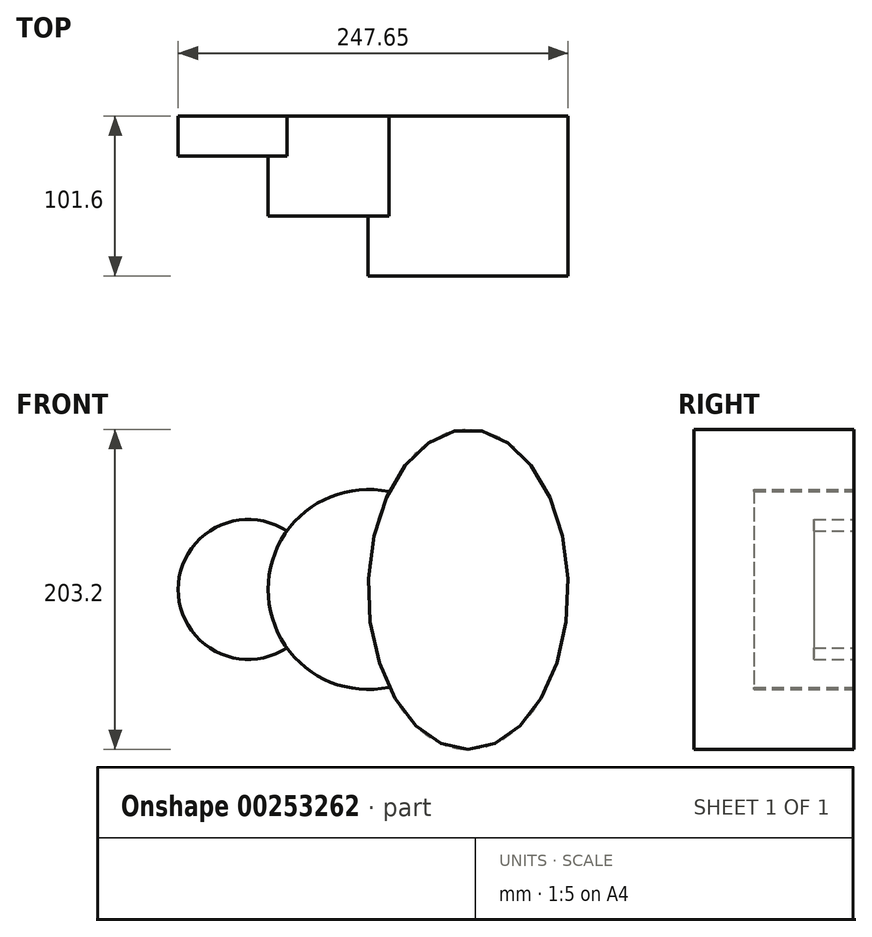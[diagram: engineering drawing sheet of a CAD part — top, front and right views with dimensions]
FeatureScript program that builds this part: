
annotation { "Feature Type Name" : "Feature", "Feature Type Description" : "" }
export const myFeature = defineFeature(function(context is Context, id is Id, definition is map)
    precondition{}
    {
        {
            var Q0;
            Q0=qCreatedBy(makeId("Front.planeOp"),FACE);
            var sketch = newSketch(context, id + "F0", { "sketchPlane" : qUnion([Q0])});
            skLineSegment(sketch, "E0", {"start": v(0, 0) * mm, "end": v(-76.2, 0) * mm, "construction": true});
            skCircle(sketch, "E1", {"center": v(-76.2, 0) * mm, "radius": 44.45 * mm});
            skPoint(sketch, "E2", {"position": v(-63.5, 0) * mm});
            skPoint(sketch, "E3", {"position": v(-31.75, 0) * mm});
            skCircle(sketch, "E4", {"center": v(0, 0) * mm, "radius": 63.5 * mm});
            skPoint(sketch, "E5", {"position": v(63.5, 0) * mm});
            skLineSegment(sketch, "E6", {"start": v(63.5, 0) * mm, "end": v(63.5, 101.6) * mm, "construction": true});
            skEllipse(sketch, "E7", {"center": v(63.5, 0) * mm, "majorRadius": 63.5 * mm, "minorRadius": 101.6 * mm, "majorAxis": v(-1, 0)});
            skSolve(sketch);
        }
        {
            var Q0;
            {var subQ0=sQuery(id+"F0.wireOp",EDGE,"E4");var subQ1=sQuery(id+"F0.wireOp",EDGE,"E1");var subQ2=makeQuery(id+"F0.imprint","INTERSECT",VERTEX,{"disambiguationData":[OD(0.0)],"derivedFrom":[subQ1,subQ0]});Q0=makeQuery(id+"F0.imprint","IMPRINT",FACE,{"disambiguationData":[TD([[makeQuery(id+"F0.imprint","IMPRINT",EDGE,{"disambiguationData":[TD([[subQ2,-1.0]])],"derivedFrom":subQ1}),1.0]])]});}
            extrude(context, id + "F1", {"entities" : qUnion([Q0]), "depth" : 25.4 * mm});
        }
        {
            var Q0;
            {var subQ0=sQuery(id+"F0.wireOp",EDGE,"E4");var subQ1=sQuery(id+"F0.wireOp",EDGE,"E1");var subQ2=makeQuery(id+"F0.imprint","INTERSECT",VERTEX,{"disambiguationData":[OD(0.0)],"derivedFrom":[subQ1,subQ0]});Q0=makeQuery(id+"F0.imprint","IMPRINT",FACE,{"disambiguationData":[TD([[makeQuery(id+"F0.imprint","IMPRINT",EDGE,{"disambiguationData":[TD([[subQ2,1.0]])],"derivedFrom":subQ1}),1.0]])]});}
            var Q1;
            {var subQ0=sQuery(id+"F0.wireOp",EDGE,"E4");var subQ1=sQuery(id+"F0.wireOp",EDGE,"E1");var subQ2=makeQuery(id+"F0.imprint","INTERSECT",VERTEX,{"disambiguationData":[OD(0.0)],"derivedFrom":[subQ1,subQ0]});Q1=makeQuery(id+"F0.imprint","IMPRINT",FACE,{"disambiguationData":[TD([[makeQuery(id+"F0.imprint","IMPRINT",EDGE,{"disambiguationData":[TD([[subQ2,1.0]])],"derivedFrom":subQ1}),-1.0]])]});}
            extrude(context, id + "F2", {"entities" : qUnion([Q0, Q1]), "operationType" : NewBodyOperationType.ADD, "depth" : 63.5 * mm});
        }
        {
            var Q0;
            {var subQ0=sQuery(id+"F0.wireOp",EDGE,"E7");var subQ1=sQuery(id+"F0.wireOp",EDGE,"E4");var subQ2=makeQuery(id+"F0.imprint","INTERSECT",VERTEX,{"disambiguationData":[OD(0.0)],"derivedFrom":[subQ1,subQ0]});Q0=makeQuery(id+"F0.imprint","IMPRINT",FACE,{"disambiguationData":[TD([[makeQuery(id+"F0.imprint","IMPRINT",EDGE,{"disambiguationData":[TD([[subQ2,1.0]])],"derivedFrom":subQ1}),1.0]])]});}
            var Q1;
            {var subQ0=sQuery(id+"F0.wireOp",EDGE,"E7");var subQ1=sQuery(id+"F0.wireOp",EDGE,"E4");var subQ2=makeQuery(id+"F0.imprint","INTERSECT",VERTEX,{"disambiguationData":[OD(0.0)],"derivedFrom":[subQ1,subQ0]});Q1=makeQuery(id+"F0.imprint","IMPRINT",FACE,{"disambiguationData":[TD([[makeQuery(id+"F0.imprint","IMPRINT",EDGE,{"disambiguationData":[TD([[subQ2,1.0]])],"derivedFrom":subQ1}),-1.0]])]});}
            extrude(context, id + "F3", {"entities" : qUnion([Q0, Q1]), "operationType" : NewBodyOperationType.ADD, "depth" : 101.6 * mm});
        }
    });
